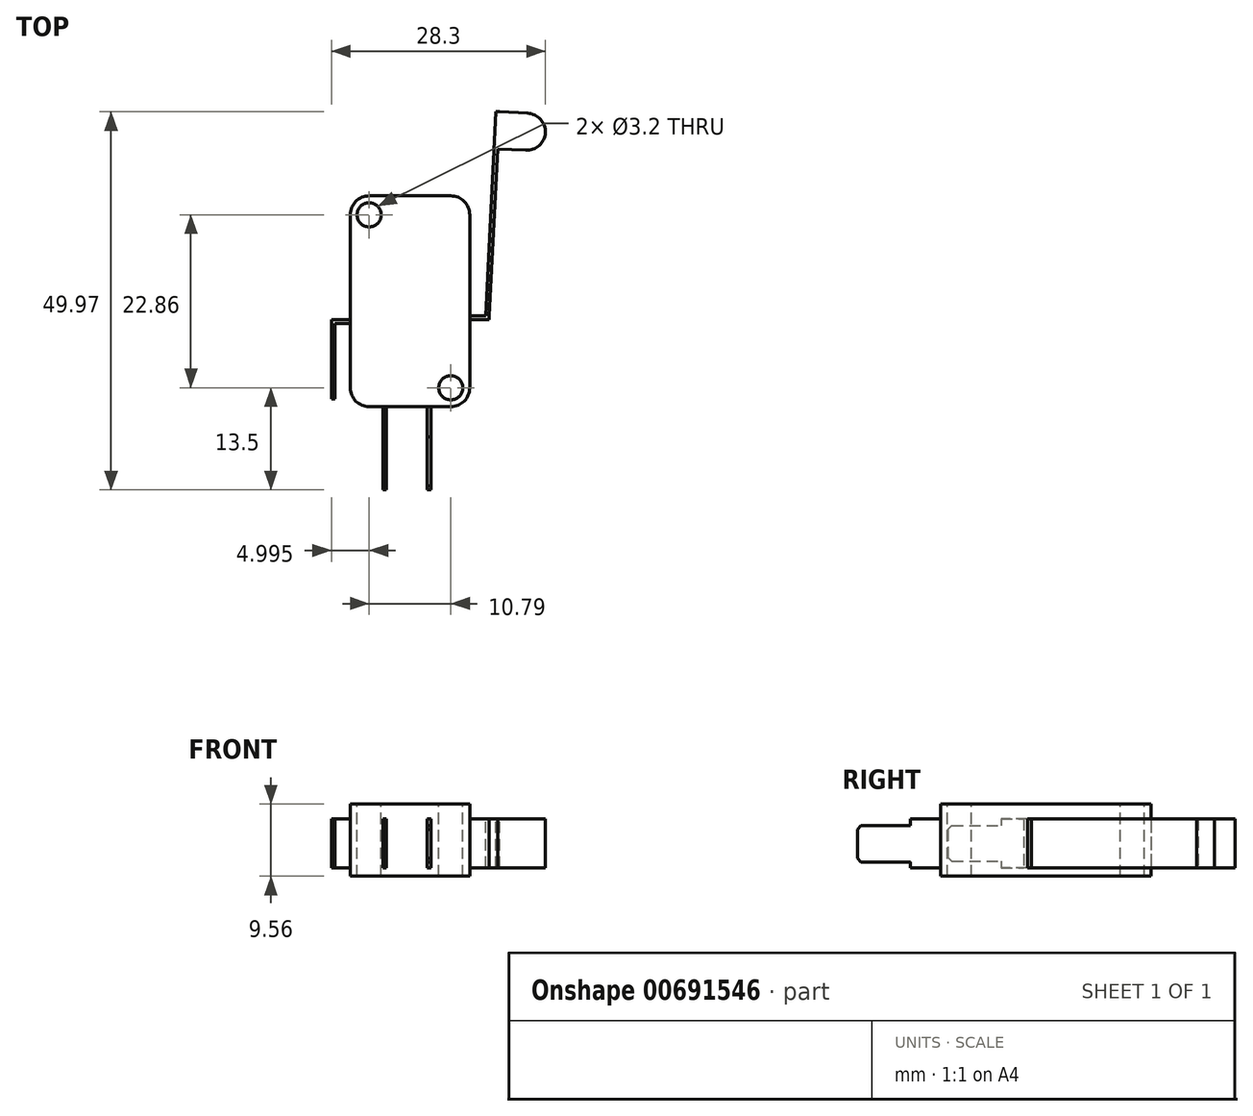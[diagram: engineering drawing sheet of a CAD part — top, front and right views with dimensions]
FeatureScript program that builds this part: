
annotation { "Feature Type Name" : "Feature", "Feature Type Description" : "" }
export const myFeature = defineFeature(function(context is Context, id is Id, definition is map)
    precondition{}
    {
        {
            var Q0;
            Q0=qCreatedBy(makeId("Top.planeOp"),FACE);
            var sketch = newSketch(context, id + "F0", { "sketchPlane" : qUnion([Q0])});
            skLineSegment(sketch, "E0.bottom", {"start": v(7.9, -13.93) * mm, "end": v(-7.9, -13.93) * mm});
            skLineSegment(sketch, "E0.top", {"start": v(7.9, 13.93) * mm, "end": v(-7.9, 13.93) * mm});
            skLineSegment(sketch, "E0.left", {"start": v(7.9, -13.93) * mm, "end": v(7.9, 13.93) * mm});
            skLineSegment(sketch, "E0.right", {"start": v(-7.9, -13.93) * mm, "end": v(-7.9, 13.93) * mm});
            skPoint(sketch, "E0.middle", {"position": v(0, 0) * mm});
            skSolve(sketch);
        }
        {
            var Q0;
            Q0=qSketchRegion(id+"F0",true);
            extrude(context, id + "F1", {"entities" : qUnion([Q0]), "depth" : 9.55 * mm, "offsetDistance" : 25 * mm});
        }
        {
            var Q0;
            Q0=makeQuery(id+"F1.opExtrude","SWEPT_EDGE",EDGE,{"disambiguationData":[OSD([sQuery(id+"F0.wireOp",EDGE,"E0.top"),sQuery(id+"F0.wireOp",EDGE,"E0.right")])]});
            var Q1;
            Q1=makeQuery(id+"F1.opExtrude","SWEPT_EDGE",EDGE,{"disambiguationData":[OSD([sQuery(id+"F0.wireOp",EDGE,"E0.top"),sQuery(id+"F0.wireOp",EDGE,"E0.left")])]});
            var Q2;
            Q2=makeQuery(id+"F1.opExtrude","SWEPT_EDGE",EDGE,{"disambiguationData":[OSD([sQuery(id+"F0.wireOp",EDGE,"E0.bottom"),sQuery(id+"F0.wireOp",EDGE,"E0.right")])]});
            var Q3;
            Q3=makeQuery(id+"F1.opExtrude","SWEPT_EDGE",EDGE,{"disambiguationData":[OSD([sQuery(id+"F0.wireOp",EDGE,"E0.bottom"),sQuery(id+"F0.wireOp",EDGE,"E0.left")])]});
            fillet(context, id + "F2", {"entities" : qUnion([Q0, Q1, Q2, Q3]), "radius" : 2.5 * mm, "tangentPropagation" : true, "allowEdgeOverflow" : false});
        }
        {
            var Q0;
            Q0=makeQuery(id+"F1.opExtrude","CAP_FACE",FACE,{"disambiguationData":[OSD([sQuery(id+"F0.wireOp",EDGE,"E0.bottom"),sQuery(id+"F0.wireOp",EDGE,"E0.top"),sQuery(id+"F0.wireOp",EDGE,"E0.left"),sQuery(id+"F0.wireOp",EDGE,"E0.right")])],"isStart":false});
            var sketch = newSketch(context, id + "F3", { "sketchPlane" : qUnion([Q0])});
            skCircle(sketch, "E1", {"center": v(-5.4, 11.43) * mm, "radius": 1.6 * mm});
            skCircle(sketch, "E2", {"center": v(5.4, -11.43) * mm, "radius": 1.6 * mm});
            skLineSegment(sketch, "E3", {"start": v(3.8, -11.43) * mm, "end": v(3.8, -13.93) * mm, "construction": true});
            skSolve(sketch);
        }
        {
            var Q0;
            Q0=qSketchRegion(id+"F3",true);
            extrude(context, id + "F4", {"entities" : qUnion([Q0]), "operationType" : NewBodyOperationType.REMOVE, "oppositeDirection" : true, "depth" : 25 * mm, "offsetDistance" : 25 * mm});
        }
        {
            var Q0;
            Q0=makeQuery(id+"F1.opExtrude","SWEPT_FACE",FACE,{"disambiguationData":[OSD([sQuery(id+"F0.wireOp",EDGE,"E0.bottom")])]});
            var sketch = newSketch(context, id + "F5", { "sketchPlane" : qUnion([Q0])});
            skLineSegment(sketch, "E4.bottom", {"start": v(-3.6, 7.55) * mm, "end": v(-3.1, 7.55) * mm});
            skLineSegment(sketch, "E4.top", {"start": v(-3.6, 1.12) * mm, "end": v(-3.1, 1.12) * mm});
            skLineSegment(sketch, "E4.left", {"start": v(-3.6, 7.55) * mm, "end": v(-3.6, 1.12) * mm});
            skLineSegment(sketch, "E4.right", {"start": v(-3.1, 7.55) * mm, "end": v(-3.1, 1.12) * mm});
            skLineSegment(sketch, "E5.bottom", {"start": v(2.3, 7.55) * mm, "end": v(2.8, 7.55) * mm});
            skLineSegment(sketch, "E5.top", {"start": v(2.3, 1.12) * mm, "end": v(2.8, 1.12) * mm});
            skLineSegment(sketch, "E5.left", {"start": v(2.3, 7.55) * mm, "end": v(2.3, 1.12) * mm});
            skLineSegment(sketch, "E5.right", {"start": v(2.8, 7.55) * mm, "end": v(2.8, 1.12) * mm});
            skLineSegment(sketch, "E6", {"start": v(3.8, 9.55) * mm, "end": v(3.8, 0) * mm, "construction": true});
            skSolve(sketch);
        }
        {
            var Q0;
            Q0=qSketchRegion(id+"F5",true);
            extrude(context, id + "F6", {"entities" : qUnion([Q0]), "operationType" : NewBodyOperationType.ADD, "depth" : 4 * mm, "offsetDistance" : 25 * mm});
        }
        {
            var Q0;
            Q0=makeQuery(id+"F6.opExtrude","CAP_FACE",FACE,{"disambiguationData":[OSD([sQuery(id+"F5.wireOp",EDGE,"E4.bottom"),sQuery(id+"F5.wireOp",EDGE,"E4.top"),sQuery(id+"F5.wireOp",EDGE,"E4.left"),sQuery(id+"F5.wireOp",EDGE,"E4.right")])],"isStart":false});
            var sketch = newSketch(context, id + "F7", { "sketchPlane" : qUnion([Q0])});
            skLineSegment(sketch, "E7.bottom", {"start": v(-3.6, 6.69) * mm, "end": v(-3.1, 6.69) * mm});
            skLineSegment(sketch, "E7.top", {"start": v(-3.6, 1.99) * mm, "end": v(-3.1, 1.99) * mm});
            skLineSegment(sketch, "E7.left", {"start": v(-3.6, 6.69) * mm, "end": v(-3.6, 1.99) * mm});
            skLineSegment(sketch, "E7.right", {"start": v(-3.1, 6.69) * mm, "end": v(-3.1, 1.99) * mm});
            skLineSegment(sketch, "E8.bottom", {"start": v(2.3, 6.69) * mm, "end": v(2.8, 6.69) * mm});
            skLineSegment(sketch, "E8.top", {"start": v(2.3, 1.87) * mm, "end": v(2.8, 1.87) * mm});
            skLineSegment(sketch, "E8.left", {"start": v(2.3, 6.69) * mm, "end": v(2.3, 1.87) * mm});
            skLineSegment(sketch, "E8.right", {"start": v(2.8, 6.69) * mm, "end": v(2.8, 1.87) * mm});
            skLineSegment(sketch, "E9", {"start": v(-3.6, 7.55) * mm, "end": v(-3.6, 6.69) * mm, "construction": true});
            skLineSegment(sketch, "E10", {"start": v(-3.6, 1.99) * mm, "end": v(-3.6, 1.12) * mm, "construction": true});
            skSolve(sketch);
        }
        {
            var Q0;
            Q0=qSketchRegion(id+"F7",true);
            extrude(context, id + "F8", {"entities" : qUnion([Q0]), "operationType" : NewBodyOperationType.ADD, "depth" : 7 * mm, "offsetDistance" : 25 * mm});
        }
        {
            var Q0;
            Q0=makeQuery(id+"F8.opExtrude","CAP_EDGE",EDGE,{"disambiguationData":[OSD([sQuery(id+"F7.wireOp",EDGE,"E7.bottom")])],"isStart":false});
            var Q1;
            Q1=makeQuery(id+"F8.opExtrude","CAP_EDGE",EDGE,{"disambiguationData":[OSD([sQuery(id+"F7.wireOp",EDGE,"E8.bottom")])],"isStart":false});
            var Q2;
            Q2=makeQuery(id+"F8.opExtrude","CAP_EDGE",EDGE,{"disambiguationData":[OSD([sQuery(id+"F7.wireOp",EDGE,"E8.top")])],"isStart":false});
            var Q3;
            Q3=makeQuery(id+"F8.opExtrude","CAP_EDGE",EDGE,{"disambiguationData":[OSD([sQuery(id+"F7.wireOp",EDGE,"E7.top")])],"isStart":false});
            chamfer(context, id + "F9", {"entities" : qUnion([Q0, Q1, Q2, Q3]), "width" : .5 * mm, "tangentPropagation" : true});
        }
        {
            var Q0;
            Q0=makeQuery(id+"F1.opExtrude","SWEPT_FACE",FACE,{"disambiguationData":[OSD([sQuery(id+"F0.wireOp",EDGE,"E0.right")])]});
            var sketch = newSketch(context, id + "F10", { "sketchPlane" : qUnion([Q0])});
            skLineSegment(sketch, "E11.bottom", {"start": v(2.43, 7.55) * mm, "end": v(2.93, 7.55) * mm});
            skLineSegment(sketch, "E11.top", {"start": v(2.43, 1.12) * mm, "end": v(2.93, 1.12) * mm});
            skLineSegment(sketch, "E11.left", {"start": v(2.43, 7.55) * mm, "end": v(2.43, 1.12) * mm});
            skLineSegment(sketch, "E11.right", {"start": v(2.93, 7.55) * mm, "end": v(2.93, 1.12) * mm});
            skSolve(sketch);
        }
        {
            var Q0;
            Q0=qSketchRegion(id+"F10",true);
            extrude(context, id + "F11", {"entities" : qUnion([Q0]), "operationType" : NewBodyOperationType.ADD, "depth" : 2.5 * mm, "offsetDistance" : 25 * mm});
        }
        {
            var Q0;
            Q0=makeQuery(id+"F11.opExtrude","SWEPT_FACE",FACE,{"disambiguationData":[OSD([sQuery(id+"F10.wireOp",EDGE,"E11.right")])]});
            var sketch = newSketch(context, id + "F12", { "sketchPlane" : qUnion([Q0])});
            skLineSegment(sketch, "E12.bottom", {"start": v(-10.4, 1.12) * mm, "end": v(-9.9, 1.12) * mm});
            skLineSegment(sketch, "E12.top", {"start": v(-10.4, 7.55) * mm, "end": v(-9.9, 7.55) * mm});
            skLineSegment(sketch, "E12.left", {"start": v(-10.4, 1.12) * mm, "end": v(-10.4, 7.55) * mm});
            skLineSegment(sketch, "E12.right", {"start": v(-9.9, 1.12) * mm, "end": v(-9.9, 7.55) * mm});
            skSolve(sketch);
        }
        {
            var Q0;
            Q0=qSketchRegion(id+"F12",true);
            extrude(context, id + "F13", {"entities" : qUnion([Q0]), "operationType" : NewBodyOperationType.ADD, "depth" : 3 * mm, "offsetDistance" : 25 * mm});
        }
        {
            var Q0;
            Q0=makeQuery(id+"F13.opExtrude","CAP_FACE",FACE,{"disambiguationData":[OSD([sQuery(id+"F12.wireOp",EDGE,"E12.bottom"),sQuery(id+"F12.wireOp",EDGE,"E12.top"),sQuery(id+"F12.wireOp",EDGE,"E12.left"),sQuery(id+"F12.wireOp",EDGE,"E12.right")])],"isStart":false});
            var sketch = newSketch(context, id + "F14", { "sketchPlane" : qUnion([Q0])});
            skLineSegment(sketch, "E13.bottom", {"start": v(-10.4, 6.69) * mm, "end": v(-9.9, 6.69) * mm});
            skLineSegment(sketch, "E13.top", {"start": v(-10.4, 1.99) * mm, "end": v(-9.9, 1.99) * mm});
            skLineSegment(sketch, "E13.left", {"start": v(-10.4, 6.69) * mm, "end": v(-10.4, 1.99) * mm});
            skLineSegment(sketch, "E13.right", {"start": v(-9.9, 6.69) * mm, "end": v(-9.9, 1.99) * mm});
            skLineSegment(sketch, "E14", {"start": v(-10.4, 7.55) * mm, "end": v(-10.4, 6.69) * mm, "construction": true});
            skLineSegment(sketch, "E15", {"start": v(-10.4, 1.99) * mm, "end": v(-10.4, 1.12) * mm, "construction": true});
            skSolve(sketch);
        }
        {
            var Q0;
            Q0=qSketchRegion(id+"F14",true);
            extrude(context, id + "F15", {"entities" : qUnion([Q0]), "operationType" : NewBodyOperationType.ADD, "depth" : 7 * mm, "offsetDistance" : 25 * mm});
        }
        {
            var Q0;
            Q0=makeQuery(id+"F15.opExtrude","CAP_EDGE",EDGE,{"disambiguationData":[OSD([sQuery(id+"F14.wireOp",EDGE,"E13.bottom")])],"isStart":false});
            var Q1;
            Q1=makeQuery(id+"F15.opExtrude","CAP_EDGE",EDGE,{"disambiguationData":[OSD([sQuery(id+"F14.wireOp",EDGE,"E13.top")])],"isStart":false});
            chamfer(context, id + "F16", {"entities" : qUnion([Q0, Q1]), "width" : .5 * mm, "tangentPropagation" : true});
        }
        {
            var Q0;
            Q0=makeQuery(id+"F1.opExtrude","SWEPT_FACE",FACE,{"disambiguationData":[OSD([sQuery(id+"F0.wireOp",EDGE,"E0.left")])]});
            var sketch = newSketch(context, id + "F17", { "sketchPlane" : qUnion([Q0])});
            skLineSegment(sketch, "E16.bottom", {"start": v(-2.43, 7.55) * mm, "end": v(-1.93, 7.55) * mm});
            skLineSegment(sketch, "E16.top", {"start": v(-2.43, 1.12) * mm, "end": v(-1.93, 1.12) * mm});
            skLineSegment(sketch, "E16.left", {"start": v(-2.43, 7.55) * mm, "end": v(-2.43, 1.12) * mm});
            skLineSegment(sketch, "E16.right", {"start": v(-1.93, 7.55) * mm, "end": v(-1.93, 1.12) * mm});
            skSolve(sketch);
        }
        {
            var Q0;
            Q0=qSketchRegion(id+"F17",true);
            extrude(context, id + "F18", {"entities" : qUnion([Q0]), "operationType" : NewBodyOperationType.ADD, "depth" : 2.6 * mm, "offsetDistance" : 25 * mm});
        }
        {
            var Q0;
            Q0=makeQuery(id+"F18.opExtrude","SWEPT_FACE",FACE,{"disambiguationData":[OSD([sQuery(id+"F17.wireOp",EDGE,"E16.bottom")])]});
            var sketch = newSketch(context, id + "F19", { "sketchPlane" : qUnion([Q0])});
            skLineSegment(sketch, "E17", {"start": v(10, -1.93) * mm, "end": v(11.34, 25.04) * mm});
            skLineSegment(sketch, "E18", {"start": v(10.5, -1.93) * mm, "end": v(11.84, 25.04) * mm});
            skLineSegment(sketch, "E19", {"start": v(11.34, 25.04) * mm, "end": v(11.84, 25.04) * mm});
            skLineSegment(sketch, "E20", {"start": v(10, -1.93) * mm, "end": v(10.5, -1.93) * mm});
            skSolve(sketch);
        }
        {
            var Q0;
            Q0=makeQuery(id+"F19.imprint","IMPRINT",FACE,{"disambiguationData":[TD([[makeQuery(id+"F19.imprint","IMPRINT",EDGE,{"derivedFrom":sQuery(id+"F19.wireOp",EDGE,"E17")}),-1.0]])]});
            var Q1;
            Q1=makeQuery(id+"F18.opExtrude","SWEPT_FACE",FACE,{"disambiguationData":[OSD([sQuery(id+"F17.wireOp",EDGE,"E16.top")])]});
            extrude(context, id + "F20", {"entities" : qUnion([Q0]), "operationType" : NewBodyOperationType.ADD, "endBound" : BoundingType.UP_TO_SURFACE, "oppositeDirection" : true, "depth" : 25 * mm, "endBoundEntityFace" : qUnion([Q1]), "offsetDistance" : 25 * mm});
        }
        {
            var Q0;
            Q0=makeQuery(id+"F20.opExtrude","SWEPT_FACE",FACE,{"disambiguationData":[OSD([sQuery(id+"F19.wireOp",EDGE,"E18")])]});
            var sketch = newSketch(context, id + "F21", { "sketchPlane" : qUnion([Q0])});
            skLineSegment(sketch, "E21.bottom", {"start": v(25.6, 7.55) * mm, "end": v(20.7, 7.55) * mm});
            skLineSegment(sketch, "E21.top", {"start": v(25.6, 1.12) * mm, "end": v(20.7, 1.12) * mm});
            skLineSegment(sketch, "E21.left", {"start": v(25.6, 7.55) * mm, "end": v(25.6, 1.12) * mm});
            skLineSegment(sketch, "E21.right", {"start": v(20.7, 7.55) * mm, "end": v(20.7, 1.12) * mm});
            skSolve(sketch);
        }
        {
            var Q0;
            Q0=qSketchRegion(id+"F21",true);
            extrude(context, id + "F22", {"entities" : qUnion([Q0]), "operationType" : NewBodyOperationType.ADD, "depth" : 6.2 * mm, "offsetDistance" : 25 * mm});
        }
        {
            var Q0;
            Q0=makeQuery(id+"F22.opExtrude","CAP_EDGE",EDGE,{"disambiguationData":[OSD([sQuery(id+"F21.wireOp",EDGE,"E21.right")])],"isStart":false});
            var Q1;
            Q1=makeQuery(id+"F22.opExtrude","CAP_EDGE",EDGE,{"disambiguationData":[OSD([sQuery(id+"F21.wireOp",EDGE,"E21.left")])],"isStart":false});
            fillet(context, id + "F23", {"entities" : qUnion([Q0, Q1]), "radius" : 2.5 * mm, "tangentPropagation" : true, "allowEdgeOverflow" : false});
        }
    });
